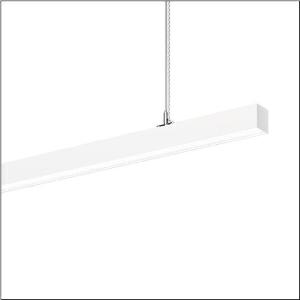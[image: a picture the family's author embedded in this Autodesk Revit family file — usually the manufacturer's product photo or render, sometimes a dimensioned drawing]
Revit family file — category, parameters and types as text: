
# Revit family: silica_r__21_51mx30db45wb_134d
name_source: partatom
category: Lighting Fixtures
units: mm (PartAtom-declared; Revit-internal decimal feet)

## family parameters
Cut with Voids When Loaded = No
Host = Face
Light Source = No
Part Type = Normal
Room Calculation Point = No
Round Connector Dimension = Use Diameter
Shared = No

## types (1)
- --- (1 x LED, 5260 lm, 32 W, 4000K)
    Apparent Load = 32 VA
    CIE Flux Codes = 47 79 96 57 100
    Color Rendering = 80
    Color Temperature = 4000K
    Default Elevation = 1800 mm
    Description = Silica® 21, office luminaire, primary optical cover: cover, of PMMA, opal, light emission: direct/indirect distribution, primary light characteristic: symmetric, installation type: suspended mounting, LED, rated luminous flux: 5.260lm, luminous efficacy: 164lm/W, light colour: 840, colour temperature: 4000K, with terminal, 3+2-pole, max. 2.5mm², mains connection: 220..240V, AC, 50/60Hz, rated input power: 32W, luminaire housing, of aluminium, traffic white (RAL 9016), length: 1.504mm, width: 53mm, height: 53mm, protection rating (complete): IP20, insulation class (complete): insulation class I (protective earthing), certification: CE, permissible operating ambient temperature: 0..+35°C, standard: EN 50419, packaging unit: 1 piece
    Height = 53 mm
    Lamp = 1 x LED
    Lamp Light Flux = 5260 lm
    Lamp Power = 32 W
    Lamp count = 1
    Length = 1504 mm
    Luminous efficacy = 164 lm/W
    Manufacturer = Siteco
    ModVariant = No
    Model = 51MX30DB45WB
    Mounting Place = Ceiling
    Mounting Type = Pendant
    Number of Poles = 1
    OnlyDefault = Yes
    Power Factor = 1
    Product Name = Silica® 21
    Product group = office luminaire | ceiling pendant
    ProductGroupID = 902
    Protection Class = Protection class I
    Protection Degree = IP 20
    RLX_Detail_Level = 1
    RLX_Emergency_Light_Flux = 0 lm
    RLX_Emergency_Type = 0
    RLX_Emergency_Type_DB = No
    RlxData = <blob elided: 21281 chars, md5=c2085ee0>
    Socket = socket
    Standby Power = 0 W
    System Light Flux = 5260 lm
    System Power = 32 W
    Type Comments = factory setting: luminous flux: 100 % | dim-lin: 254 | 218 mA
    Type Image = l_1313629.jpg
    URL = http://relux.com
    VarID = @adj_065007
    Voltage = 0 V
    Weight = 0.00 kg
    Width = 53 mm

## geometry (parser evidence)
native form markers: Blend x4, Sweep x12
no freeform markers — native parametric forms only
